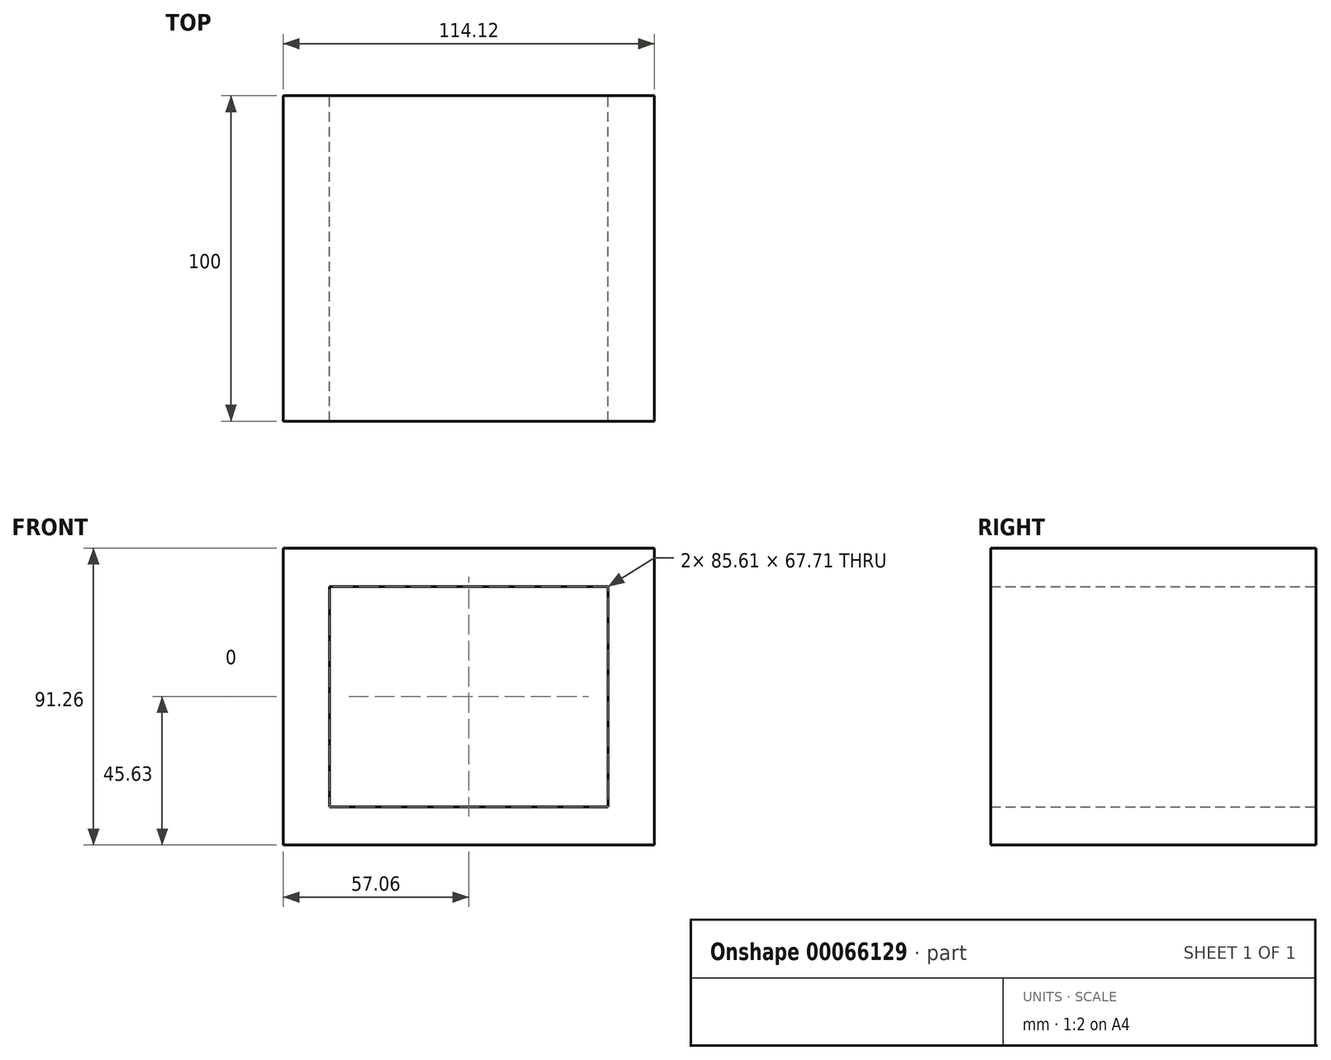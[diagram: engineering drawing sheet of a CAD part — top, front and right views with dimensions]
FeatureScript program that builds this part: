
annotation { "Feature Type Name" : "Feature", "Feature Type Description" : "" }
export const myFeature = defineFeature(function(context is Context, id is Id, definition is map)
    precondition{}
    {
        {
            var Q0;
            Q0=qCreatedBy(makeId("Front.planeOp"),FACE);
            var sketch = newSketch(context, id + "F0", { "sketchPlane" : qUnion([Q0])});
            skLineSegment(sketch, "E0.rect.bottom", {"start": v(-42.8, 33.85) * mm, "end": v(42.8, 33.85) * mm});
            skLineSegment(sketch, "E0.rect.top", {"start": v(-42.8, -33.85) * mm, "end": v(42.8, -33.85) * mm});
            skLineSegment(sketch, "E0.rect.left", {"start": v(-42.8, 33.85) * mm, "end": v(-42.8, -33.85) * mm});
            skLineSegment(sketch, "E0.rect.right", {"start": v(42.8, 33.85) * mm, "end": v(42.8, -33.85) * mm});
            skPoint(sketch, "E0.rect.middle", {"position": v(0, 0) * mm});
            skLineSegment(sketch, "E1.rect.bottom", {"start": v(57.06, 45.63) * mm, "end": v(-57.06, 45.63) * mm});
            skLineSegment(sketch, "E1.rect.top", {"start": v(57.06, -45.63) * mm, "end": v(-57.06, -45.63) * mm});
            skLineSegment(sketch, "E1.rect.left", {"start": v(57.06, 45.63) * mm, "end": v(57.06, -45.63) * mm});
            skLineSegment(sketch, "E1.rect.right", {"start": v(-57.06, 45.63) * mm, "end": v(-57.06, -45.63) * mm});
            skSolve(sketch);
        }
        {
            var Q0;
            Q0 = qSketchRegion(id + "F0", true);
            extrude(context, id + "F1", {"entities" : qUnion([Q0]), "depth" : 100 * mm});
        }
    });
